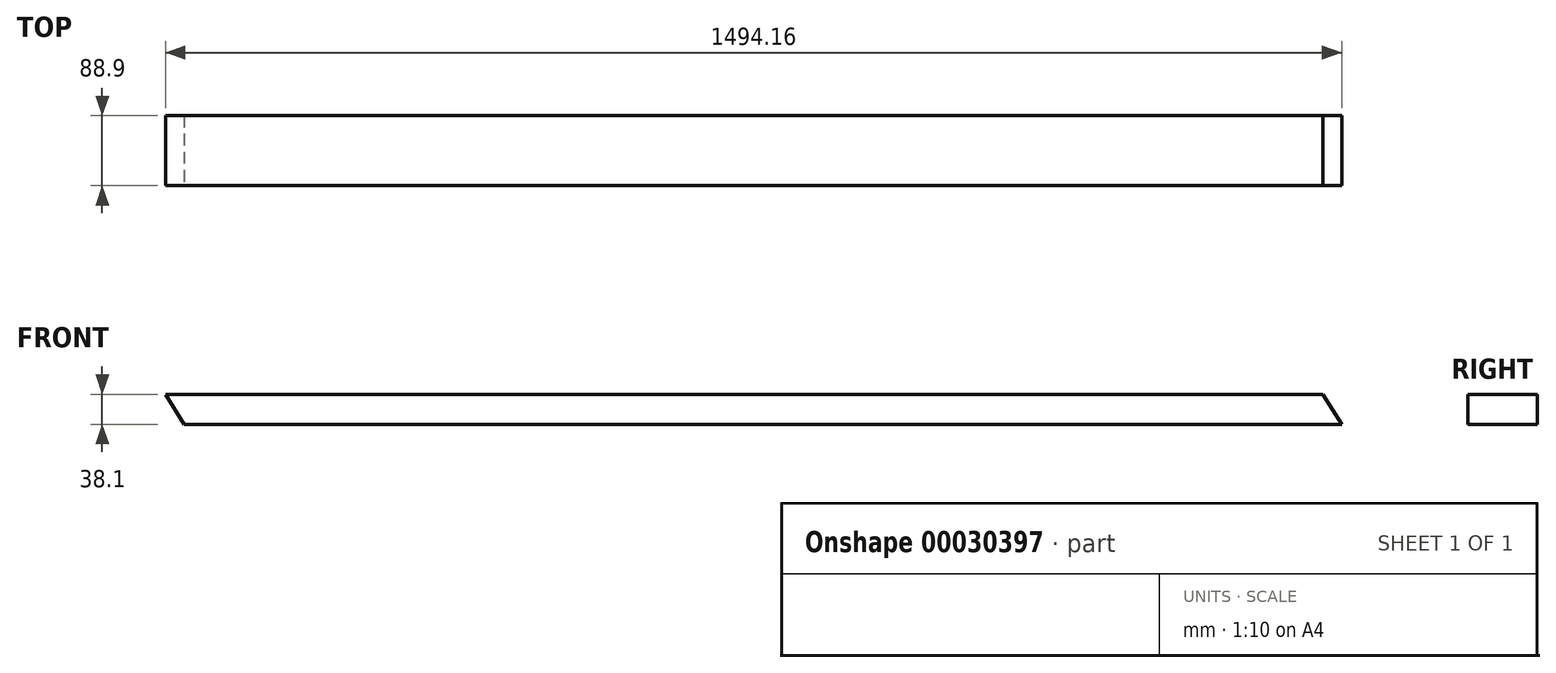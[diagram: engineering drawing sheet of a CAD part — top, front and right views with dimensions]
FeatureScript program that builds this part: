
annotation { "Feature Type Name" : "Feature", "Feature Type Description" : "" }
export const myFeature = defineFeature(function(context is Context, id is Id, definition is map)
    precondition{}
    {
        {
            var Q0;
            Q0=qCreatedBy(makeId("Top.planeOp"),FACE);
            var sketch = newSketch(context, id + "F0", { "sketchPlane" : qUnion([Q0])});
            skLineSegment(sketch, "E0.rect.left", {"start": v(747.08, 44.45) * mm, "end": v(747.08, -44.45) * mm});
            skLineSegment(sketch, "E0.rect.right", {"start": v(-747.08, 44.45) * mm, "end": v(-747.08, -44.45) * mm});
            skPoint(sketch, "E0.rect.middle", {"position": v(0, 0) * mm});
            skLineSegment(sketch, "E1", {"start": v(747.08, 44.45) * mm, "end": v(543.05, 44.45) * mm});
            skLineSegment(sketch, "E2", {"start": v(-747.08, 44.45) * mm, "end": v(543.05, 44.45) * mm});
            skLineSegment(sketch, "E3", {"start": v(-747.08, -44.45) * mm, "end": v(-691, -44.45) * mm});
            skLineSegment(sketch, "E4", {"start": v(747.08, -44.45) * mm, "end": v(-691, -44.45) * mm});
            skSolve(sketch);
        }
        {
            var Q0;
            Q0=qSketchRegion(id+"F0",true);
            extrude(context, id + "F1", {"entities" : qUnion([Q0]), "endBound" : BoundingType.SYMMETRIC, "depth" : 38.1 * mm});
        }
        {
            var Q0;
            Q0=qCreatedBy(makeId("Front.planeOp"),FACE);
            var sketch = newSketch(context, id + "F2", { "sketchPlane" : qUnion([Q0])});
            skLineSegment(sketch, "E5", {"start": v(747.08, -19.05) * mm, "end": v(723.05, 19.05) * mm});
            skLineSegment(sketch, "E6", {"start": v(-723.05, -19.05) * mm, "end": v(-747.08, 19.05) * mm});
            skLineSegment(sketch, "E7", {"start": v(-747.08, 19.05) * mm, "end": v(-747.08, -19.05) * mm});
            skLineSegment(sketch, "E8", {"start": v(-747.08, -19.05) * mm, "end": v(-723.05, -19.05) * mm});
            skLineSegment(sketch, "E9", {"start": v(723.05, 19.05) * mm, "end": v(747.08, 19.05) * mm});
            skLineSegment(sketch, "E10", {"start": v(747.08, 19.05) * mm, "end": v(747.08, -19.05) * mm});
            skSolve(sketch);
        }
        {
            var Q0;
            Q0 = qSketchRegion(id + "F2", true);
            extrude(context, id + "F3", {"entities" : qUnion([Q0]), "operationType" : NewBodyOperationType.REMOVE, "endBound" : BoundingType.THROUGH_ALL, "oppositeDirection" : true, "depth" : 25.4 * mm, "hasSecondDirection" : true, "secondDirectionBound" : SecondDirectionBoundingType.THROUGH_ALL, "secondDirectionOppositeDirection" : false, "secondDirectionDepth" : 25.4 * mm});
        }
    });
